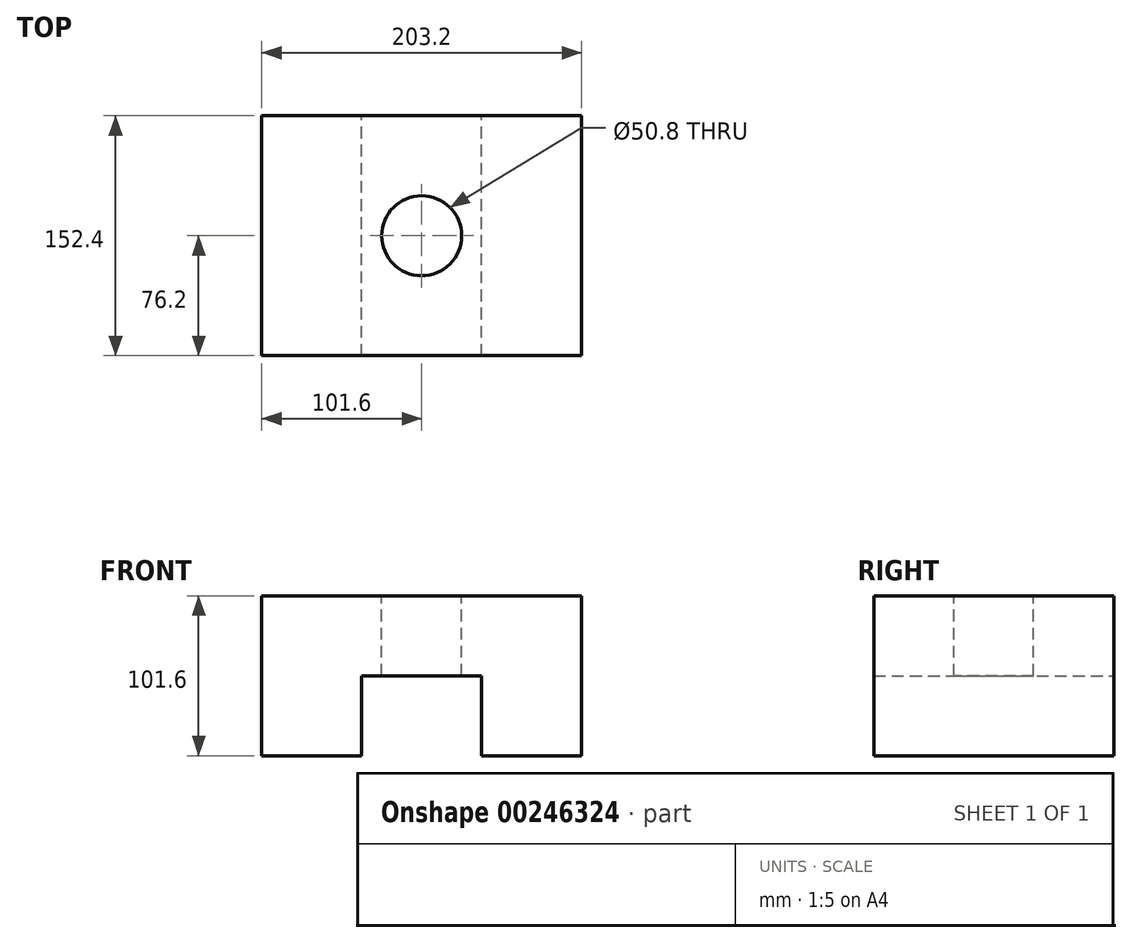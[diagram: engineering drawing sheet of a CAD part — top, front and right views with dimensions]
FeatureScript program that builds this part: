
annotation { "Feature Type Name" : "Feature", "Feature Type Description" : "" }
export const myFeature = defineFeature(function(context is Context, id is Id, definition is map)
    precondition{}
    {
        {
            var Q0;
            Q0=qCreatedBy(makeId("Front.planeOp"),FACE);
            var sketch = newSketch(context, id + "F0", { "sketchPlane" : qUnion([Q0])});
            skLineSegment(sketch, "E0.bottom", {"start": v(0, 0) * mm, "end": v(63.5, 0) * mm});
            skLineSegment(sketch, "E0.top", {"start": v(0, 101.6) * mm, "end": v(203.2, 101.6) * mm});
            skLineSegment(sketch, "E0.left", {"start": v(0, 0) * mm, "end": v(0, 101.6) * mm});
            skLineSegment(sketch, "E0.right", {"start": v(203.2, 0) * mm, "end": v(203.2, 101.6) * mm});
            skLineSegment(sketch, "E1", {"start": v(63.5, 0) * mm, "end": v(63.5, 50.8) * mm});
            skLineSegment(sketch, "E2", {"start": v(63.5, 50.8) * mm, "end": v(139.7, 50.8) * mm});
            skLineSegment(sketch, "E3", {"start": v(139.7, 50.8) * mm, "end": v(139.7, 0) * mm});
            skLineSegment(sketch, "E4.trimOffspring", {"start": v(139.7, 0) * mm, "end": v(203.2, 0) * mm});
            skSolve(sketch);
        }
        {
            var Q0;
            Q0=makeQuery(id+"F0.imprint","IMPRINT",FACE,{"disambiguationData":[TD([[makeQuery(id+"F0.imprint","IMPRINT",EDGE,{"derivedFrom":sQuery(id+"F0.wireOp",EDGE,"E0.bottom")}),1.0]])]});
            extrude(context, id + "F1", {"entities" : qUnion([Q0]), "depth" : 152.4 * mm});
        }
        {
            var Q0;
            Q0=makeQuery(id+"F1.opExtrude","SWEPT_FACE",FACE,{"disambiguationData":[OSD([sQuery(id+"F0.wireOp",EDGE,"E0.top")])]});
            var sketch = newSketch(context, id + "F2", { "sketchPlane" : qUnion([Q0])});
            skCircle(sketch, "E5", {"center": v(101.6, -76.2) * mm, "radius": 25.4 * mm});
            skSolve(sketch);
        }
        {
            var Q0;
            Q0=makeQuery(id+"F2.imprint","IMPRINT",FACE,{"disambiguationData":[TD([[makeQuery(id+"F2.imprint","IMPRINT",EDGE,{"derivedFrom":sQuery(id+"F2.wireOp",EDGE,"E5")}),1.0]])]});
            extrude(context, id + "F3", {"entities" : qUnion([Q0]), "operationType" : NewBodyOperationType.REMOVE, "endBound" : BoundingType.THROUGH_ALL, "oppositeDirection" : true, "depth" : 25.4 * mm});
        }
    });
